# Revit family: OASIS SH-5038 STD
name_source: partatom
category: Plumbing Fixtures
units: mm (PartAtom-declared; Revit-internal decimal feet)

## family parameters
Always vertical = Yes
Cut with Voids When Loaded = No
OmniClass Number = 23.45.05.14.21.11
OmniClass Title = Bath/Shower Units
Part Type = Normal
Room Calculation Point = No
Round Connector Dimension = Use Diameter
Shared = No
Work Plane-Based = No

## types (7) — shared parameters
BIM Model By = www.shive-hattery.com
Cold Water Connector = Cold Water Connection
Color = <By Category>
Default Elevation = 0"
Grab Bar Finish = <By Category>
Hot Water Connector = Hot Water Connection
Manufacturer = OASIS
Sanitary Connector = Sanitary Connection
Seat Finish = <By Category>
Shower Rod = No
Stainless steel = <By Category>
Type Comments = Shower
URL = www.oasisbath.com

## per-type parameters (varying)
| type | Bar_Horz_Back | Bar_Horz_Left | Bar_Horz_Right | Bar_Vert | Model | Seat_Fold |
| Base Model, 3SF, 3SM, & FH Packages | No | No | No | No | SH-5038 STD/(Base Model,3SF,3SM,FH) | No |
| BP2 Package | Yes | Yes | No | Yes | SH-5038 STD/BP2 | No |
| BP5 Package | Yes | No | No | No | SH-5038 STD/BP5 | No |
| TL Package | Yes | Yes | No | No | SH-5038 STD/TL | Yes |
| TLV Package | Yes | Yes | No | Yes | SH-5038 STD/TLV | Yes |
| BP3 Package | Yes | Yes | Yes | No | SH-5038 STD/BP3 | No |
| BP1 Package | Yes | Yes | No | No | SH-5038 STD/BP1 | No |

## geometry (parser evidence)
native form markers: Sweep x10
no freeform markers — native parametric forms only
